# Revit family: Remeha_QuintaAce160_4Boilers-LowLossHeaders-FreeStanding-LOD3
name_source: partatom
category: Mechanical Equipment
revit_build: Autodesk Revit 2017 (Build: 20190508_0315(x64)
units: mm (PartAtom-declared; Revit-internal decimal feet)

## family parameters
Always vertical = Yes
Cut with Voids When Loaded = Yes
OmniClass Number = 23.75.10.11.14
OmniClass Title = Hot Water Heat Generators
Part Type = Normal
Room Calculation Point = No
Round Connector Dimension = Use Diameter
Shared = No
Work Plane-Based = No

## types (2) — shared parameters
Access Clearance Bottom = 0.00 mm
Access Clearance Front = 1000.00 mm
Access Clearance Left = 600.00 mm
Access Clearance Rear = 0.00 mm
Access Clearance Right = 600.00 mm
Access Clearance Top = 500.00 mm
Annually = As Per Attached URL O&M Manual
BMS Links = Yes
Boiler Spacing = 630.00 mm
Building Regulations Seasonal Efficiency = 95.9
Burner Control Type = Modulating
CE Mark = Yes
Colour = RAL 9016
Condensate Drain Size = 32.00 mm
Condensate Drain Type = Plain
Configuration = Cascade boilers
Control Type = '0 - 10V, Open Therm, Volt free enable, Direct boiler weather compensating control systems available from Remeha as optional extra's.
Dirt Separator Visibility = Yes
Drain Connection Size = 15.00 mm
Drain Connection Type = Threaded
Energy Technology List = https://etl.beis.gov.uk
ErP Energy Label = 0
ErP Rated Efficiency at Full Load = 87.8
ErP Rated Efficiency at Part Load = 97.8
ErP Seasonal Efficiency = 0
Expected Life = 15
External Material = Steel
Features = Remeha's Quinta Ace Cascade systems consist of high efficiency wall hung condensing boilers, high output and more efficient, making them ideally suited to modular arrangements.
Finish = High PolishGardner 60 Grad 91EH
Flow and Return Connection Size = 125.00 mm
Flow and Return Connection Type = Flanged
Flue or Air Intake Classification = B23p, C13, C33, C53,
Frequency = 50 Hz
Fuel Connection Size = 65.00 mm
Fuel Connection Type = Flanged
Full Load Current = 0 A
Fuse Rating = 6 A
Gas Consumption rate = 66.0
Gross Weight = 1221.00 kg
Heat Exchanger Material = Aluminium
Heater Operation = Condensing
Hydraulic Resistance at 11C temperature differential = 0.00000
Hydraulic Resistance at 20C temperature differential = 0.17000
IK Rating = Not Required
IP Rating = IPX1B
IfcExportAs = IfcBoilerType
IfcExportType = NOTDEFINED
Insulation Visibility = Yes
Interlocks = Yes
Load Classification = Power
Manufacturer = Remeha
Manufacturer Website = www.remeha.co.uk
Maximum Gas Inlet Pressure = 0.02500 bar
Maximum Oil Inlet Pressure = 0.00000 bar
Maximum Operating Pressure = 4.00000 bar
Maximum Power Consumption = 275 W
Minimum Flow Rate at 11C temperature differential = 0.0 L/s
Minimum Flow Rate at 20C temperature differential = 1.8 L/s
Minimum Gas Inlet Pressure = 0.01700 bar
Minimum Oil Inlet Pressure = 0.00000 bar
Minimum Operating Pressure = 0.80000 bar
Minimum Power Consumption = 47 W
Mounting = Floor Standing
NOx Emissions = 36
No Of Boilers = 4
Nominal Gas Inlet Pressure = 0.02000 bar
Nominal Oil Inlet Pressure = 0.00000 bar
Operation and Maintenance Manual = https://www.remeha.co.uk
Overall Height = 2003.50 mm
Overall Length = 676.00 mm
Overall Width = 3213.00 mm
Primary Fuel = Gas - NG
Product Literature = https://www.remeha.co.uk
Product Model Number = KTS00255
Product Range = Quinta Ace 160 Cascade Floor Standing 4 X Quinta Ace 160 with standard low loss header
Rated Criteria = 80/60
Rated Output = 608400 W
Reference Standard = (EU) 2016/426
Safety Valve Connection Size = 20.00 mm
Safety Valve Connection Type = Threaded
Shape = Rectangular (Vertical)
Shipping Weight = 0.00 kg
Sound Pressure Level = 59.5
Starting Current = 0 A
Supply Phase = 1
Turndown Ratio = 4.88:1
Type = Space heating
Voltage = 230 V
Water Content = 179.0 L
Water Treatment Required = Yes
zero-valued in all types: Oil Consumption rate

## per-type parameters (varying)
| type | Flue Connection size |
| 100/150 Concentric Flue Connection - 150 Connector | 150.00 mm |
| 100/150 Conventional Flue Connection - 100 Connector | 100.00 mm |

note: source unit labels omitted for Hydraulic Resistance at 11C temperature differential, Hydraulic Resistance at 20C temperature differential — the stored unit's dimension contradicts the parameter name (converter mislabeling)

## geometry (parser evidence)
native form markers: Blend x2, Sweep x24
no freeform markers — native parametric forms only
